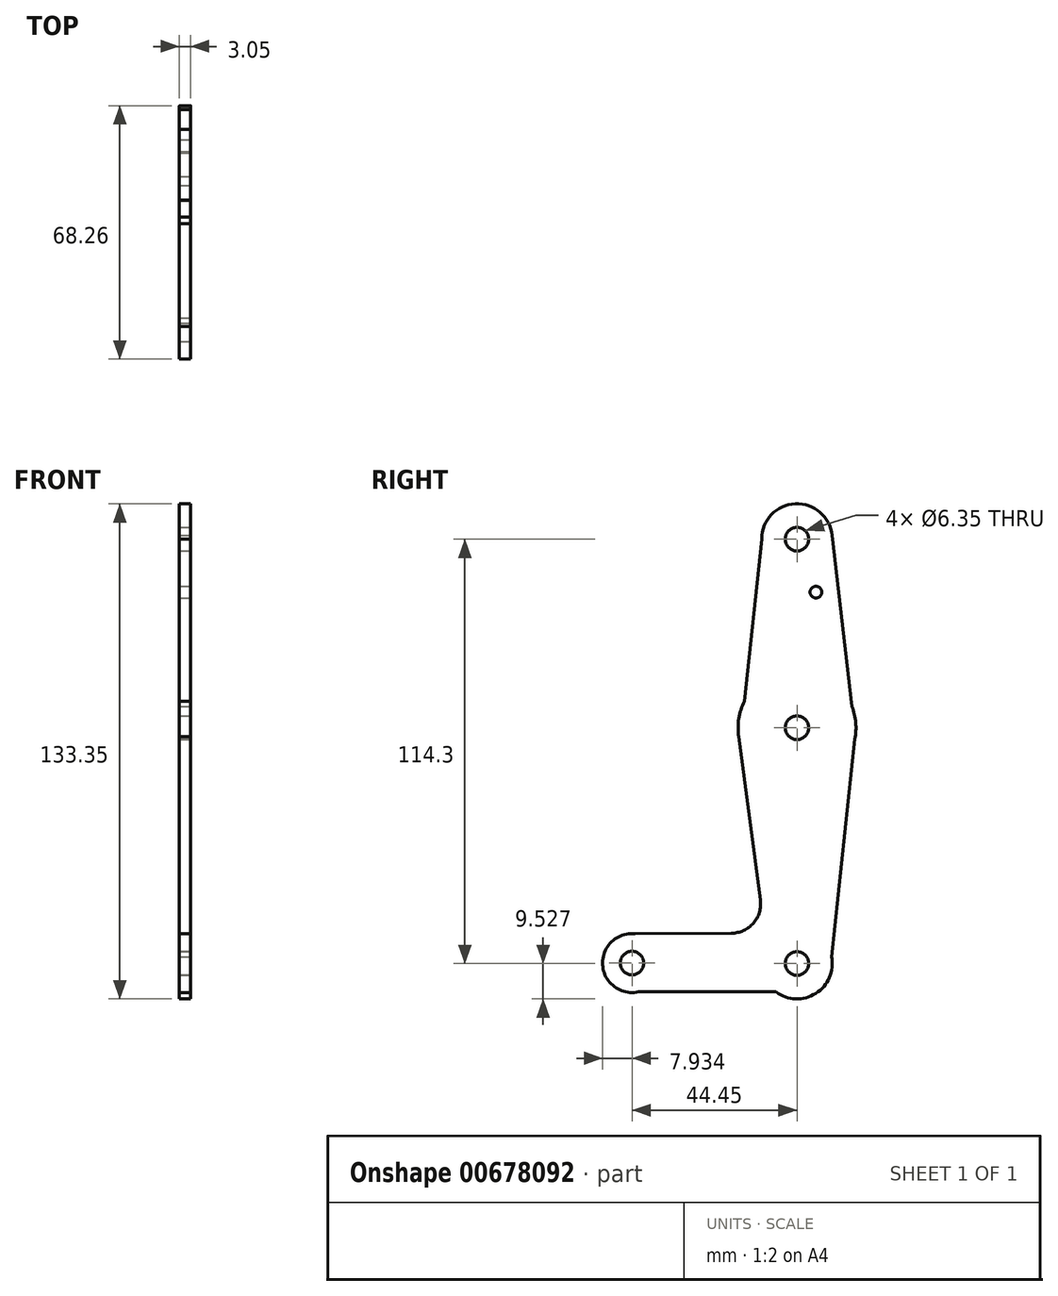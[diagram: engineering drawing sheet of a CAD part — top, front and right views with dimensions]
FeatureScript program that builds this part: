
annotation { "Feature Type Name" : "Feature", "Feature Type Description" : "" }
export const myFeature = defineFeature(function(context is Context, id is Id, definition is map)
    precondition{}
    {
        {
            var Q0;
            Q0=qCreatedBy(makeId("Right.planeOp"),FACE);
            var sketch = newSketch(context, id + "F0", { "sketchPlane" : qUnion([Q0])});
            skLineSegment(sketch, "E0", {"start": v(30.14, 94.47) * mm, "end": v(30.14, -19.83) * mm});
            skLineSegment(sketch, "E1", {"start": v(-14.3, -19.73) * mm, "end": v(30.14, -19.83) * mm});
            skCircle(sketch, "E2", {"center": v(30.14, 94.47) * mm, "radius": 9.53 * mm});
            skCircle(sketch, "E3", {"center": v(30.14, 43.67) * mm, "radius": 15.88 * mm});
            skCircle(sketch, "E4", {"center": v(30.14, -19.83) * mm, "radius": 9.53 * mm});
            skCircle(sketch, "E5", {"center": v(-14.3, -19.73) * mm, "radius": 7.94 * mm});
            skLineSegment(sketch, "E6", {"start": v(39.6, 95.67) * mm, "end": v(44.96, 49.37) * mm});
            skLineSegment(sketch, "E7", {"start": v(20.62, 94.54) * mm, "end": v(15.98, 50.83) * mm});
            skLineSegment(sketch, "E8", {"start": v(39.5, -18.02) * mm, "end": v(46.02, 43.37) * mm});
            skLineSegment(sketch, "E9", {"start": v(20.29, -2.69) * mm, "end": v(14.36, 41.95) * mm});
            skLineSegment(sketch, "E10", {"start": v(12.45, -11.69) * mm, "end": v(-13.51, -11.83) * mm});
            skLineSegment(sketch, "E11", {"start": v(24.46, -27.48) * mm, "end": v(-12.58, -27.48) * mm});
            skCircle(sketch, "E12", {"center": v(30.14, 94.47) * mm, "radius": 3.18 * mm});
            skCircle(sketch, "E13", {"center": v(35.25, 80.2) * mm, "radius": 1.59 * mm});
            skCircle(sketch, "E14", {"center": v(30.14, 43.67) * mm, "radius": 3.18 * mm});
            skCircle(sketch, "E15", {"center": v(30.14, -19.83) * mm, "radius": 3.18 * mm});
            skCircle(sketch, "E16", {"center": v(-14.3, -19.73) * mm, "radius": 3.18 * mm});
            skArc(sketch, "E17.filletArc", {"start": v(12.45, -11.69) * mm, "mid": v(18.4, -8.96) * mm, "end": v(20.29, -2.69) * mm});
            skSolve(sketch);
        }
        {
            var Q0;
            Q0 = qSketchRegion(id + "F0", true);
            var Q1;
            {var subQ0=sQuery(id+"F0.wireOp",EDGE,"E4");var subQ1=sQuery(id+"F0.wireOp",EDGE,"E0");var subQ2=makeQuery(id+"F0.imprint","INTERSECT",VERTEX,{"derivedFrom":[subQ1,subQ0]});Q1=makeQuery(id+"F0.imprint","IMPRINT",FACE,{"disambiguationData":[TD([[makeQuery(id+"F0.imprint","IMPRINT",EDGE,{"disambiguationData":[TD([[subQ2,-1.0]])],"derivedFrom":subQ1}),-1.0]])]});}
            extrude(context, id + "F1", {"entities" : qUnion([Q0, Q1]), "oppositeDirection" : true, "depth" : 3.05 * mm, "offsetDistance" : 25.4 * mm});
        }
    });
